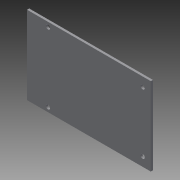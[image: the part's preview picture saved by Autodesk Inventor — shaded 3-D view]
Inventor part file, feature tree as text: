
AUTODESK INVENTOR PART (.ipt)
format: ipt  version: 2014 (Build 180170000, 170)  size: 95,232 bytes
history: native  units: mm
features: sketch x2, other x1, extrude x1, hole x1
ambient origin geometry x8: Origin, YZ Plane, XZ Plane, XY Plane, X Axis, Y Axis, Z Axis, Center Point
bodies: Body1 (feature_tree)
feature tree (5):
  other  "ソリッド1"
  extrude  "押し出し1"  Depth=86.36mm
  hole  "穴1"  [1 undecoded]
  sketch  "スケッチ1"
  sketch  "スケッチ2"
note: 1 required parameter value undecoded (feature->parameter linkage not recoverable at this tier; creation-order binding heuristic only, values carry confidence <= 0.55)
